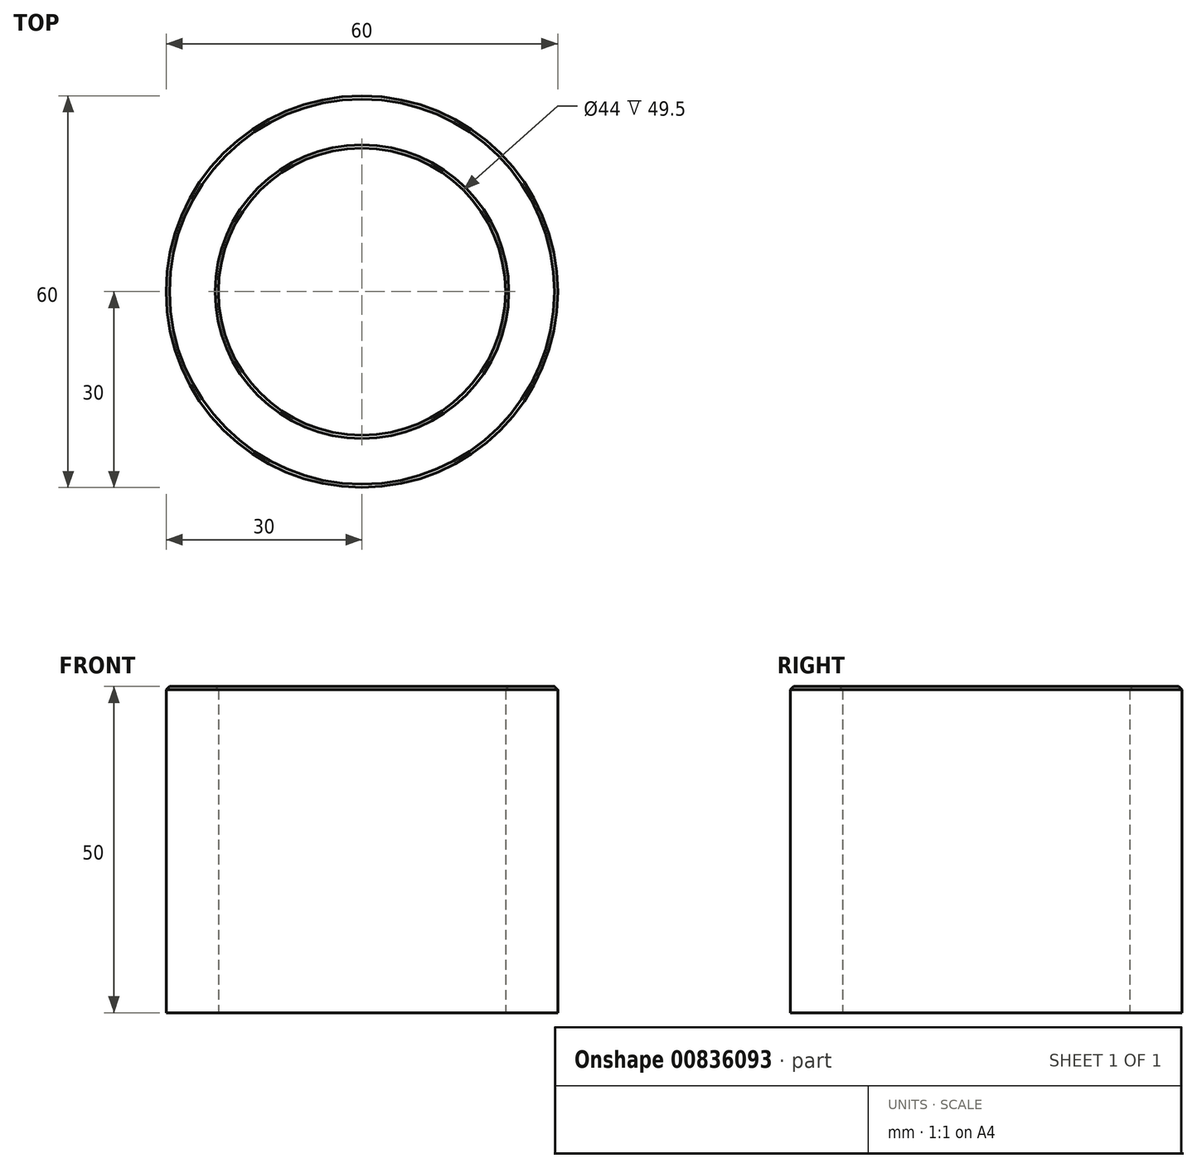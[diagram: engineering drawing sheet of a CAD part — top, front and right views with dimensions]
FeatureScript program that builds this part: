
annotation { "Feature Type Name" : "Feature", "Feature Type Description" : "" }
export const myFeature = defineFeature(function(context is Context, id is Id, definition is map)
    precondition{}
    {
        {
            var Q0;
            Q0=qCreatedBy(makeId("Top.planeOp"),FACE);
            var sketch = newSketch(context, id + "F0", { "sketchPlane" : qUnion([Q0])});
            skCircle(sketch, "E0", {"center": v(0, 0) * mm, "radius": 30 * mm});
            skCircle(sketch, "E1", {"center": v(0, 0) * mm, "radius": 22 * mm});
            skSolve(sketch);
        }
        {
            var Q0;
            Q0=makeQuery(id+"F0.imprint","IMPRINT",FACE,{"disambiguationData":[TD([[makeQuery(id+"F0.imprint","IMPRINT",EDGE,{"derivedFrom":sQuery(id+"F0.wireOp",EDGE,"E0")}),1.0]])]});
            extrude(context, id + "F1", {"entities" : qUnion([Q0]), "depth" : 50 * mm, "offsetDistance" : 25 * mm});
        }
        {
            var Q0;
            Q0=makeQuery(id+"F1.opExtrude","CAP_EDGE",EDGE,{"disambiguationData":[OSD([sQuery(id+"F0.wireOp",EDGE,"E0")])],"isStart":false});
            chamfer(context, id + "F2", {"entities" : qUnion([Q0]), "width" : 0.5 * mm, "tangentPropagation" : true});
        }
        {
            var Q0;
            Q0=makeQuery(id+"F1.opExtrude","CAP_EDGE",EDGE,{"disambiguationData":[OSD([sQuery(id+"F0.wireOp",EDGE,"E1")])],"isStart":false});
            chamfer(context, id + "F3", {"entities" : qUnion([Q0]), "width" : 0.5 * mm, "tangentPropagation" : true});
        }
    });
